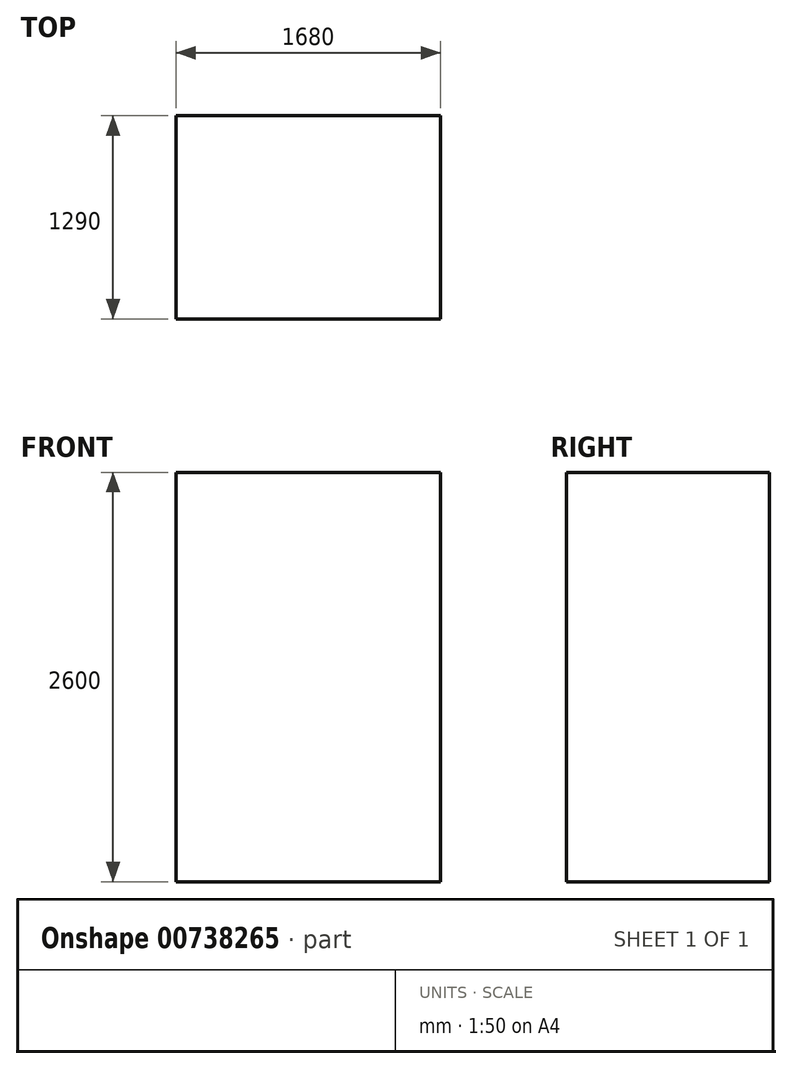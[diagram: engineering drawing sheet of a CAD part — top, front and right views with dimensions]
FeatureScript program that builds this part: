
annotation { "Feature Type Name" : "Feature", "Feature Type Description" : "" }
export const myFeature = defineFeature(function(context is Context, id is Id, definition is map)
    precondition{}
    {
        {
            var Q0;
            Q0=qCreatedBy(makeId("Top.planeOp"),FACE);
            var sketch = newSketch(context, id + "F0", { "sketchPlane" : qUnion([Q0])});
            skLineSegment(sketch, "E0.bottom", {"start": v(840, -645) * mm, "end": v(-840, -645) * mm});
            skLineSegment(sketch, "E0.top", {"start": v(840, 645) * mm, "end": v(-840, 645) * mm});
            skLineSegment(sketch, "E0.left", {"start": v(840, -645) * mm, "end": v(840, 645) * mm});
            skLineSegment(sketch, "E0.right", {"start": v(-840, -645) * mm, "end": v(-840, 645) * mm});
            skPoint(sketch, "E0.middle", {"position": v(0, 0) * mm});
            skSolve(sketch);
        }
        {
            var Q0;
            Q0=makeQuery(id+"F0.imprint","IMPRINT",FACE,{"disambiguationData":[TD([[makeQuery(id+"F0.imprint","IMPRINT",EDGE,{"derivedFrom":sQuery(id+"F0.wireOp",EDGE,"E0.bottom")}),-1.0]])]});
            extrude(context, id + "F1", {"entities" : qUnion([Q0]), "depth" : 2600 * mm, "offsetDistance" : 25 * mm});
        }
    });
